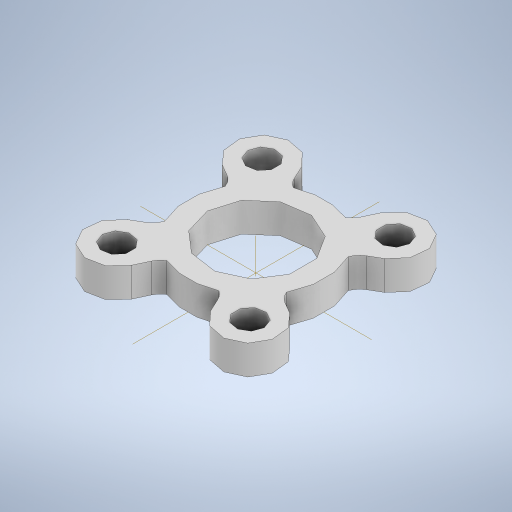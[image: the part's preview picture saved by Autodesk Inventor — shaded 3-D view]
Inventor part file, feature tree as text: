
AUTODESK INVENTOR PART (.ipt)
format: ipt  version: 2024.2 (Build 282272000, 272)  size: 295,936 bytes
history: native  units: mm
features: extrude x2, mirror x2, other x1, sketch x1
ambient origin geometry x8: Origin, YZ Plane, XZ Plane, XY Plane, X Axis, Y Axis, Z Axis, Center Point
bodies: Body1 (feature_tree)
feature tree (6):
  other  "Твердое тело1"
  sketch  "Эскиз1"
  extrude  "Выдавливание1"  Depth=10.0mm
  extrude  "Выдавливание2"  Depth=6.0mm
  mirror  "Зеркальное отражение1"
  mirror  "Зеркальное отражение2"
